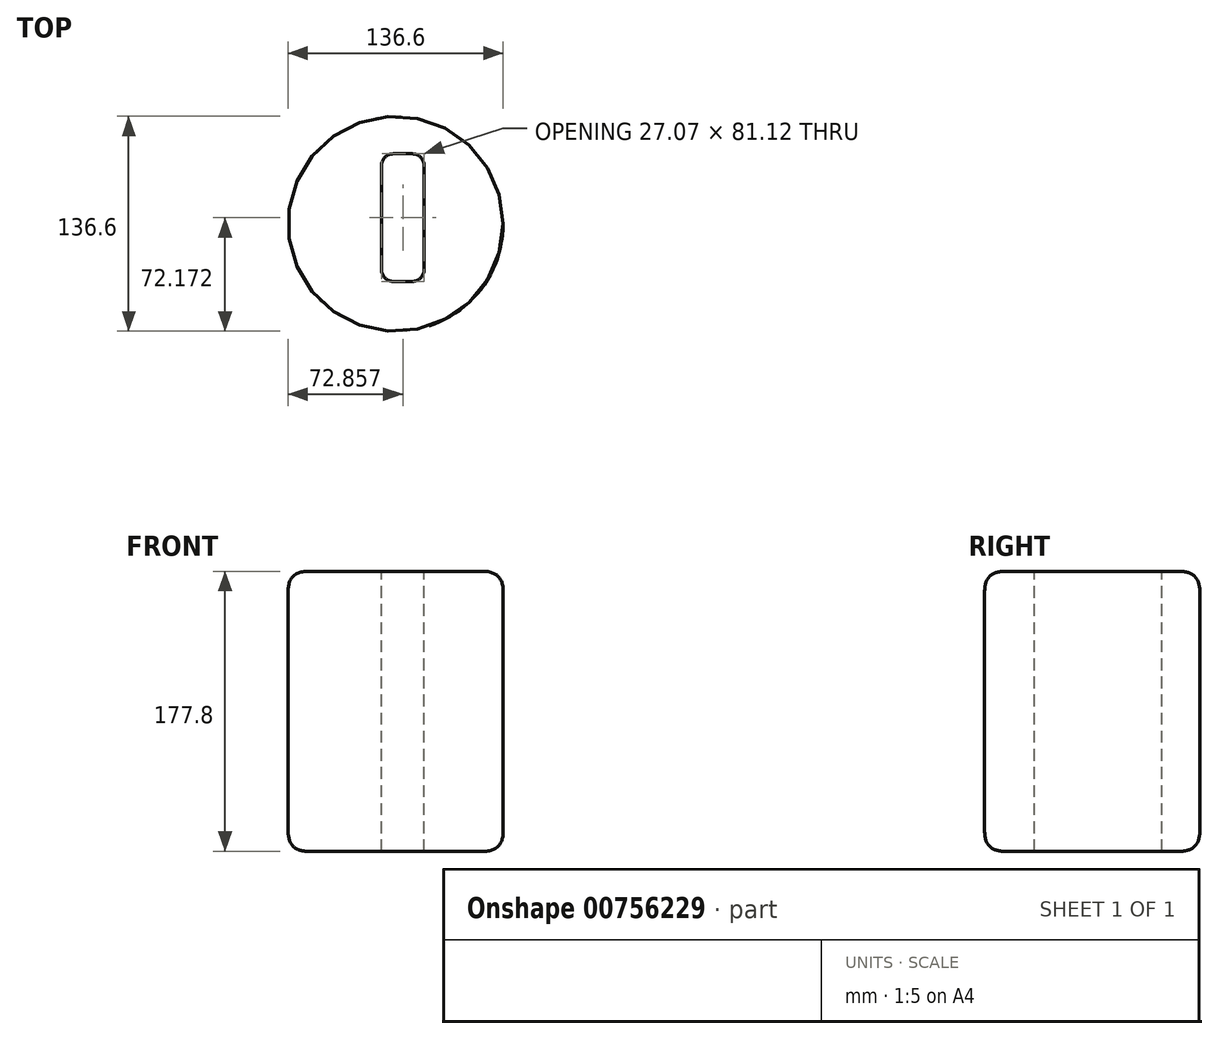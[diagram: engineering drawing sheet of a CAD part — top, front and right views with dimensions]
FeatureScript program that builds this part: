
annotation { "Feature Type Name" : "Feature", "Feature Type Description" : "" }
export const myFeature = defineFeature(function(context is Context, id is Id, definition is map)
    precondition{}
    {
        {
            var Q0;
            Q0=qCreatedBy(makeId("Top.planeOp"),FACE);
            var sketch = newSketch(context, id + "F0", { "sketchPlane" : qUnion([Q0])});
            skCircle(sketch, "E0", {"center": v(0, 0) * mm, "radius": 68.3 * mm});
            skSolve(sketch);
        }
        {
            var Q0;
            Q0 = qSketchRegion(id + "F0", true);
            extrude(context, id + "F1", {"entities" : qUnion([Q0]), "depth" : 101.6 * mm, "offsetDistance" : 25.4 * mm, "hasSecondDirection" : true, "secondDirectionOppositeDirection" : true, "secondDirectionDepth" : 76.2 * mm});
        }
        {
            var Q0;
            Q0=makeQuery(id+"F1.opExtrude","CAP_FACE",FACE,{"disambiguationData":[OSD([sQuery(id+"F0.wireOp",EDGE,"E0")])],"isStart":false});
            var sketch = newSketch(context, id + "F2", { "sketchPlane" : qUnion([Q0])});
            skLineSegment(sketch, "E1.bottom", {"start": v(-8.98, -36.69) * mm, "end": v(18.1, -36.69) * mm});
            skLineSegment(sketch, "E1.top", {"start": v(-8.98, 44.43) * mm, "end": v(18.1, 44.43) * mm});
            skLineSegment(sketch, "E1.left", {"start": v(-8.98, -36.69) * mm, "end": v(-8.98, 44.43) * mm});
            skLineSegment(sketch, "E1.right", {"start": v(18.1, -36.69) * mm, "end": v(18.1, 44.43) * mm});
            skSolve(sketch);
        }
        {
            var Q0;
            Q0 = qSketchRegion(id + "F2", true);
            extrude(context, id + "F3", {"entities" : qUnion([Q0]), "operationType" : NewBodyOperationType.REMOVE, "endBound" : BoundingType.THROUGH_ALL, "oppositeDirection" : true, "depth" : 275.52 * mm, "offsetDistance" : 25.4 * mm});
        }
        {
            var Q0;
            Q0=makeQuery(id+"F1.opExtrude","CAP_EDGE",EDGE,{"disambiguationData":[OSD([sQuery(id+"F0.wireOp",EDGE,"E0")])],"isStart":false});
            var Q1;
            Q1=makeQuery(id+"F1.opExtrude","CAP_EDGE",EDGE,{"disambiguationData":[OSD([sQuery(id+"F0.wireOp",EDGE,"E0")])],"isStart":true});
            fillet(context, id + "F4", {"entities" : qUnion([Q0, Q1]), "radius" : 12.7 * mm, "tangentPropagation" : true, "rho" : 0.5, "crossSection" : FilletCrossSection.CONIC, "allowEdgeOverflow" : false});
        }
        {
            var Q0;
            Q0=makeQuery(id+"F3.boolean.opBoolean","COPY",EDGE,{"derivedFrom":makeQuery(id+"F3.opExtrude","SWEPT_EDGE",EDGE,{"disambiguationData":[OSD([sQuery(id+"F2.wireOp",EDGE,"E1.top"),sQuery(id+"F2.wireOp",EDGE,"E1.right")])]})});
            var Q1;
            Q1=makeQuery(id+"F3.boolean.opBoolean","COPY",EDGE,{"derivedFrom":makeQuery(id+"F3.opExtrude","SWEPT_EDGE",EDGE,{"disambiguationData":[OSD([sQuery(id+"F2.wireOp",EDGE,"E1.top"),sQuery(id+"F2.wireOp",EDGE,"E1.left")])]})});
            var Q2;
            Q2=makeQuery(id+"F3.boolean.opBoolean","COPY",EDGE,{"derivedFrom":makeQuery(id+"F3.opExtrude","SWEPT_EDGE",EDGE,{"disambiguationData":[OSD([sQuery(id+"F2.wireOp",EDGE,"E1.bottom"),sQuery(id+"F2.wireOp",EDGE,"E1.right")])]})});
            var Q3;
            Q3=makeQuery(id+"F3.boolean.opBoolean","COPY",EDGE,{"derivedFrom":makeQuery(id+"F3.opExtrude","SWEPT_EDGE",EDGE,{"disambiguationData":[OSD([sQuery(id+"F2.wireOp",EDGE,"E1.bottom"),sQuery(id+"F2.wireOp",EDGE,"E1.left")])]})});
            fillet(context, id + "F5", {"entities" : qUnion([Q0, Q1, Q2, Q3]), "radius" : 7.62 * mm, "tangentPropagation" : true, "allowEdgeOverflow" : false});
        }
        {
            var Q0;
            Q0=qCreatedBy(makeId("Front.planeOp"),FACE);
            var sketch = newSketch(context, id + "F6", { "sketchPlane" : qUnion([Q0])});
            skFitSpline(sketch, "E2", {"points": [v(0, 150.48) * mm, v(285.47, 207.96) * mm, v(359.15, -42.92) * mm, v(142.53, -98.13) * mm, v(99.62, -234.53) * mm, v(0, -147.56) * mm], "startDerivative": vector(1827.7, -1.15) * mm, "endDerivative": vector(-1364.76, 39.33) * mm});
            skLineSegment(sketch, "E3", {"start": v(0, -147.56) * mm, "end": v(0, 150.48) * mm, "construction": true});
            skLineSegment(sketch, "E4", {"start": v(-56.35, 150.48) * mm, "end": v(0, 150.48) * mm, "construction": true});
            skSolve(sketch);
        }
        {
            var Q0;
            Q0 = qSketchRegion(id + "F6", true);
            var Q1;
            Q1=sQuery(id+"F6.wireOp",EDGE,"E2");
            var Q2;
            Q2=sQuery(id+"F6.wireOp",EDGE,"E3");
            revolve(context, id + "F7", {"bodyType" : ToolBodyType.SURFACE, "surfaceOperationType" : NewSurfaceOperationType.NEW, "entities" : qUnion([Q0]), "surfaceEntities" : qUnion([Q1]), "axis" : qUnion([Q2]), "revolveType" : RevolveType.FULL});
        }
    });
